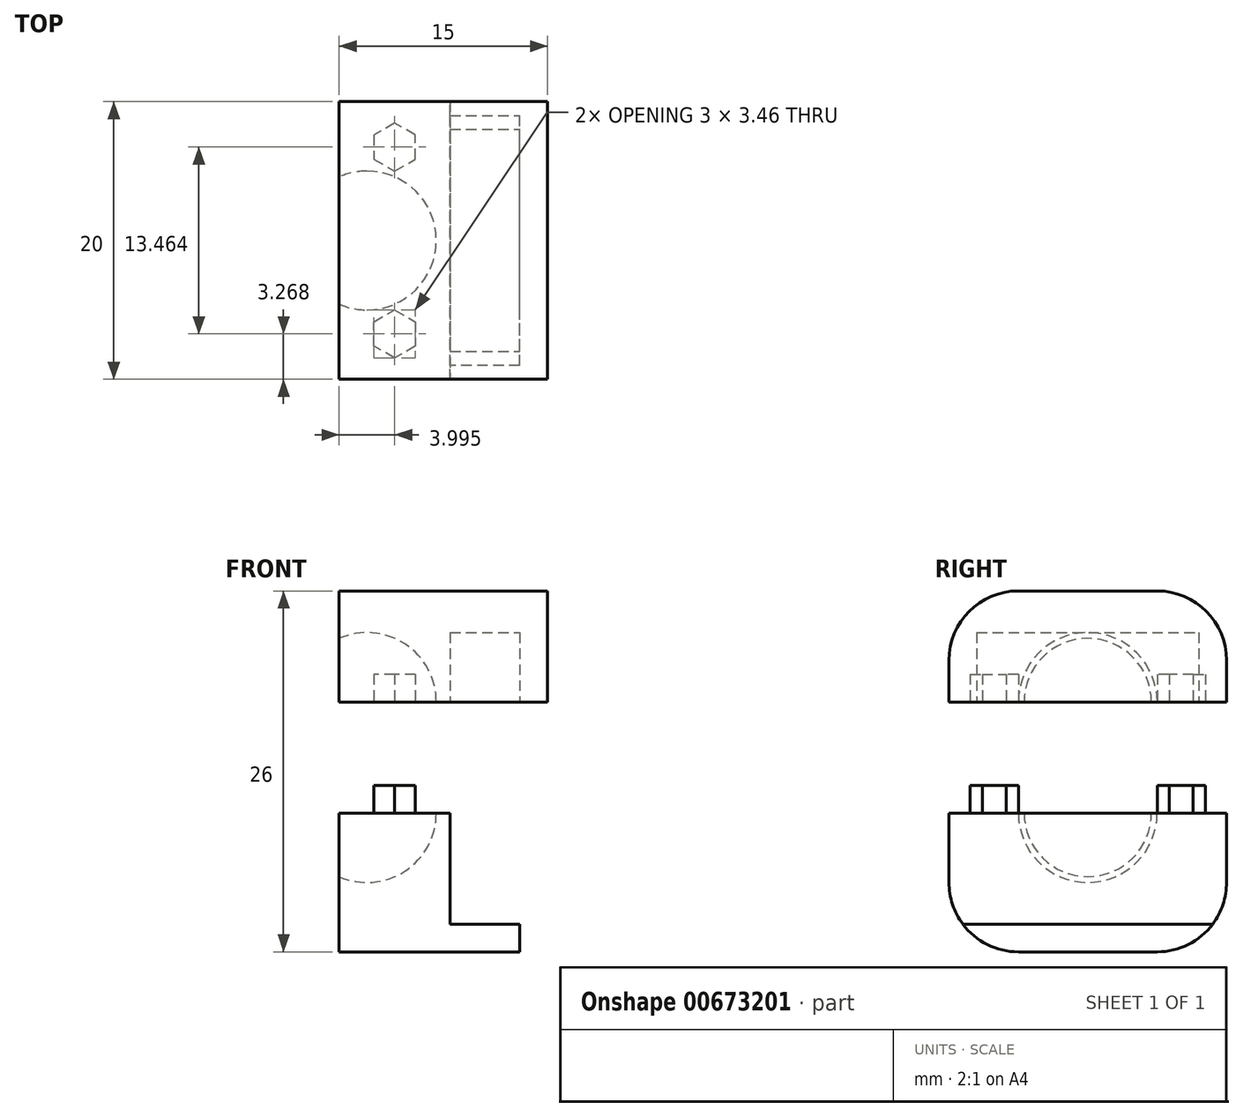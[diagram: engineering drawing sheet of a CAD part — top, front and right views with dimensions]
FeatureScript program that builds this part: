
annotation { "Feature Type Name" : "Feature", "Feature Type Description" : "" }
export const myFeature = defineFeature(function(context is Context, id is Id, definition is map)
    precondition{}
    {
        {
            var Q0;
            Q0=qCreatedBy(makeId("Top.planeOp"),FACE);
            var sketch = newSketch(context, id + "F0", { "sketchPlane" : qUnion([Q0])});
            skLineSegment(sketch, "E0.bottom", {"start": v(-4.65, 0) * mm, "end": v(10.35, 0) * mm});
            skLineSegment(sketch, "E0.top", {"start": v(-4.65, -20) * mm, "end": v(10.35, -20) * mm});
            skLineSegment(sketch, "E0.left", {"start": v(-4.65, 0) * mm, "end": v(-4.65, -20) * mm});
            skLineSegment(sketch, "E0.right", {"start": v(10.35, 0) * mm, "end": v(10.35, -20) * mm});
            skLineSegment(sketch, "E1", {"start": v(10.35, 0) * mm, "end": v(3.35, 0) * mm, "construction": true});
            skLineSegment(sketch, "E2", {"start": v(3.35, 0) * mm, "end": v(3.35, -20) * mm});
            skLineSegment(sketch, "E3", {"start": v(3.35, -20) * mm, "end": v(8.35, -20) * mm, "construction": true});
            skLineSegment(sketch, "E4", {"start": v(8.35, -20) * mm, "end": v(8.35, 0) * mm});
            skLineSegment(sketch, "E5", {"start": v(3.35, 0) * mm, "end": v(3.35, -2) * mm, "construction": true});
            skLineSegment(sketch, "E6", {"start": v(3.35, -2) * mm, "end": v(8.35, -2) * mm});
            skLineSegment(sketch, "E7", {"start": v(10.35, -10) * mm, "end": v(16.36, -10) * mm, "construction": true});
            skLineSegment(sketch, "E8.MirrorCS", {"start": v(3.35, -18) * mm, "end": v(8.35, -18) * mm});
            skLineSegment(sketch, "E9", {"start": v(-4.65, -10) * mm, "end": v(-2.65, -10) * mm, "construction": true});
            skPoint(sketch, "E9.endSnap0", {"position": v(3.35, -10) * mm});
            skArc(sketch, "E10", {"start": v(-4.65, -14.58) * mm, "mid": v(2.35, -10) * mm, "end": v(-4.65, -5.42) * mm});
            skLineSegment(sketch, "E11", {"start": v(-2.65, -15) * mm, "end": v(-2.65, -5) * mm});
            skLineSegment(sketch, "E12", {"start": v(-4.65, -20) * mm, "end": v(-0.65, -20) * mm, "construction": true});
            skLineSegment(sketch, "E13.0", {"start": v(-2.15, -17.6) * mm, "end": v(-2.15, -15.87) * mm});
            skLineSegment(sketch, "E13.1", {"start": v(-2.15, -15.87) * mm, "end": v(-0.65, -15) * mm});
            skLineSegment(sketch, "E13.2", {"start": v(-0.65, -15) * mm, "end": v(0.85, -15.87) * mm});
            skLineSegment(sketch, "E13.3", {"start": v(0.85, -15.87) * mm, "end": v(0.85, -17.6) * mm});
            skLineSegment(sketch, "E13.4", {"start": v(0.85, -17.6) * mm, "end": v(-0.65, -18.46) * mm});
            skLineSegment(sketch, "E13.5", {"start": v(-0.65, -18.46) * mm, "end": v(-2.15, -17.6) * mm});
            skPoint(sketch, "E13.0.midPoint", {"position": v(-2.15, -16.73) * mm});
            skLineSegment(sketch, "E14.MirrorCS", {"start": v(-2.15, -2.4) * mm, "end": v(-2.15, -4.13) * mm});
            skLineSegment(sketch, "E15.MirrorCS", {"start": v(0.85, -2.4) * mm, "end": v(-0.65, -1.54) * mm});
            skLineSegment(sketch, "E16.MirrorCS", {"start": v(-2.15, -4.13) * mm, "end": v(-0.65, -5) * mm});
            skLineSegment(sketch, "E17.MirrorCS", {"start": v(0.85, -4.13) * mm, "end": v(0.85, -2.4) * mm});
            skPoint(sketch, "E18.MirrorP", {"position": v(-2.15, -3.27) * mm});
            skLineSegment(sketch, "E19.MirrorCS", {"start": v(-0.65, -1.54) * mm, "end": v(-2.15, -2.4) * mm});
            skLineSegment(sketch, "E20.MirrorCS", {"start": v(-0.65, -5) * mm, "end": v(0.85, -4.13) * mm});
            skSolve(sketch);
        }
        {
            var Q0;
            Q0=qSketchRegion(id+"F0",true);
            var Q1;
            {var subQ0=sQuery(id+"F0.wireOp",EDGE,"E6");Q1=makeQuery(id+"F0.imprint","IMPRINT",FACE,{"disambiguationData":[TD([[makeQuery(id+"F0.imprint","IMPRINT",EDGE,{"derivedFrom":subQ0}),-1.0]])]});}
            var Q2;
            {var subQ0=sQuery(id+"F0.wireOp",EDGE,"E11");Q2=makeQuery(id+"F0.imprint","IMPRINT",FACE,{"disambiguationData":[TD([[makeQuery(id+"F0.imprint","IMPRINT",EDGE,{"derivedFrom":subQ0}),-1.0]])]});}
            var Q3;
            Q3=makeQuery(id+"F0.imprint","IMPRINT",FACE,{"disambiguationData":[TD([[makeQuery(id+"F0.imprint","IMPRINT",EDGE,{"derivedFrom":sQuery(id+"F0.wireOp",EDGE,"E13.0")}),-1.0]])]});
            var Q4;
            Q4=makeQuery(id+"F0.imprint","IMPRINT",FACE,{"disambiguationData":[TD([[makeQuery(id+"F0.imprint","IMPRINT",EDGE,{"derivedFrom":sQuery(id+"F0.wireOp",EDGE,"E14.MirrorCS")}),1.0]])]});
            extrude(context, id + "F1", {"entities" : qUnion([Q0, Q1, Q2, Q3, Q4]), "depth" : 6 * mm});
        }
        {
            var Q0;
            {var subQ0=sQuery(id+"F0.wireOp",EDGE,"E6");Q0=makeQuery(id+"F0.imprint","IMPRINT",FACE,{"disambiguationData":[TD([[makeQuery(id+"F0.imprint","IMPRINT",EDGE,{"derivedFrom":subQ0}),-1.0]])]});}
            extrude(context, id + "F2", {"entities" : qUnion([Q0]), "operationType" : NewBodyOperationType.REMOVE, "depth" : 5 * mm});
        }
        {
            var Q0;
            {var subQ0=sQuery(id+"F0.wireOp",EDGE,"E11");Q0=makeQuery(id+"F0.imprint","IMPRINT",FACE,{"disambiguationData":[TD([[makeQuery(id+"F0.imprint","IMPRINT",EDGE,{"derivedFrom":subQ0}),-1.0]])]});}
            var Q1;
            Q1=sQuery(id+"F0.wireOp",EDGE,"E11");
            revolve(context, id + "F3", {"operationType" : NewBodyOperationType.REMOVE, "entities" : qUnion([Q0]), "axis" : qUnion([Q1]), "revolveType" : RevolveType.FULL, "oppositeDirection" : true});
        }
        {
            var Q0;
            Q0=makeQuery(id+"F0.imprint","IMPRINT",FACE,{"disambiguationData":[TD([[makeQuery(id+"F0.imprint","IMPRINT",EDGE,{"derivedFrom":sQuery(id+"F0.wireOp",EDGE,"E13.0")}),-1.0]])]});
            var Q1;
            Q1=makeQuery(id+"F0.imprint","IMPRINT",FACE,{"disambiguationData":[TD([[makeQuery(id+"F0.imprint","IMPRINT",EDGE,{"derivedFrom":sQuery(id+"F0.wireOp",EDGE,"E14.MirrorCS")}),1.0]])]});
            extrude(context, id + "F4", {"entities" : qUnion([Q0, Q1]), "operationType" : NewBodyOperationType.REMOVE, "depth" : 2 * mm});
        }
        {
            var Q0;
            Q0=qCreatedBy(makeId("Top.planeOp"),FACE);
            cPlane(context, id + "F5", {"entities" : qUnion([Q0]), "cplaneType" : CPlaneType.OFFSET, "offset" : 4 * mm, "oppositeDirection" : true, "width" : 150 * mm, "height" : 150 * mm});
        }
        {
            var Q0;
            Q0=makeQuery(id+"F1.opExtrude","SWEPT_BODY",BODY,{"disambiguationData":[OSD([sQuery(id+"F0.wireOp",EDGE,"E0.bottom"),sQuery(id+"F0.wireOp",EDGE,"E0.top"),sQuery(id+"F0.wireOp",EDGE,"E0.left"),sQuery(id+"F0.wireOp",EDGE,"E0.right")])]});
            var Q1;
            Q1=qCreatedBy(id+"F5.planeOp",FACE);
            mirror(context, id + "F6", {"entities" : qUnion([Q0]), "mirrorPlane" : qUnion([Q1])});
        }
        {
            var Q0;
            Q0=makeQuery(id+"F6.opPattern","COPY",FACE,{"derivedFrom":makeQuery(id+"F1.opExtrude","CAP_FACE",FACE,{"disambiguationData":[OSD([sQuery(id+"F0.wireOp",EDGE,"E0.bottom"),sQuery(id+"F0.wireOp",EDGE,"E0.top"),sQuery(id+"F0.wireOp",EDGE,"E0.left"),sQuery(id+"F0.wireOp",EDGE,"E0.right")])],"isStart":true}),"instanceName":"1"});
            var sketch = newSketch(context, id + "F7", { "sketchPlane" : qUnion([Q0])});
            skLineSegment(sketch, "E21.bottom", {"start": v(3.35, 0) * mm, "end": v(10.35, 0) * mm});
            skLineSegment(sketch, "E21.top", {"start": v(3.35, -20) * mm, "end": v(10.35, -20) * mm});
            skLineSegment(sketch, "E21.left", {"start": v(3.35, 0) * mm, "end": v(3.35, -20) * mm});
            skLineSegment(sketch, "E21.right", {"start": v(10.35, 0) * mm, "end": v(10.35, -20) * mm});
            skSolve(sketch);
        }
        {
            var Q0;
            Q0=qSketchRegion(id+"F7",true);
            extrude(context, id + "F8", {"entities" : qUnion([Q0]), "operationType" : NewBodyOperationType.REMOVE, "endBound" : BoundingType.THROUGH_ALL, "oppositeDirection" : true, "depth" : 25 * mm});
        }
        {
            var Q0;
            Q0=makeQuery(id+"F6.opPattern","COPY",FACE,{"derivedFrom":makeQuery(id+"F4.boolean.opBoolean","COPY",FACE,{"derivedFrom":makeQuery(id+"F4.opExtrude","CAP_FACE",FACE,{"disambiguationData":[OSD([sQuery(id+"F0.wireOp",EDGE,"E14.MirrorCS"),sQuery(id+"F0.wireOp",EDGE,"E15.MirrorCS"),sQuery(id+"F0.wireOp",EDGE,"E16.MirrorCS"),sQuery(id+"F0.wireOp",EDGE,"E17.MirrorCS"),sQuery(id+"F0.wireOp",EDGE,"E19.MirrorCS"),sQuery(id+"F0.wireOp",EDGE,"E20.MirrorCS")])],"isStart":false})}),"instanceName":"1"});
            var Q1;
            Q1=makeQuery(id+"F6.opPattern","COPY",FACE,{"derivedFrom":makeQuery(id+"F4.boolean.opBoolean","COPY",FACE,{"derivedFrom":makeQuery(id+"F4.opExtrude","CAP_FACE",FACE,{"disambiguationData":[OSD([sQuery(id+"F0.wireOp",EDGE,"E13.0"),sQuery(id+"F0.wireOp",EDGE,"E13.1"),sQuery(id+"F0.wireOp",EDGE,"E13.2"),sQuery(id+"F0.wireOp",EDGE,"E13.3"),sQuery(id+"F0.wireOp",EDGE,"E13.4"),sQuery(id+"F0.wireOp",EDGE,"E13.5")])],"isStart":false})}),"instanceName":"1"});
            extrude(context, id + "F9", {"entities" : qUnion([Q0, Q1]), "operationType" : NewBodyOperationType.ADD, "depth" : 4 * mm});
        }
        {
            var Q0;
            Q0=makeQuery(id+"F6.opPattern","COPY",FACE,{"derivedFrom":makeQuery(id+"F1.opExtrude","CAP_FACE",FACE,{"disambiguationData":[OSD([sQuery(id+"F0.wireOp",EDGE,"E0.bottom"),sQuery(id+"F0.wireOp",EDGE,"E0.top"),sQuery(id+"F0.wireOp",EDGE,"E0.left"),sQuery(id+"F0.wireOp",EDGE,"E0.right")])],"isStart":false}),"instanceName":"1"});
            extrude(context, id + "F10", {"entities" : qUnion([Q0]), "operationType" : NewBodyOperationType.ADD, "depth" : 2 * mm});
        }
        {
            var Q0;
            Q0=makeQuery(id+"F10.opExtrude","CAP_FACE",FACE,{"disambiguationData":[OSD([sQuery(id+"F0.wireOp",EDGE,"E0.bottom"),sQuery(id+"F0.wireOp",EDGE,"E0.top"),sQuery(id+"F0.wireOp",EDGE,"E0.left"),sQuery(id+"F0.wireOp",EDGE,"E0.right")])],"isStart":false});
            extrude(context, id + "F11", {"entities" : qUnion([Q0]), "operationType" : NewBodyOperationType.ADD, "depth" : 2 * mm});
        }
        {
            var Q0;
            {var subQ0=sQuery(id+"F7.wireOp",EDGE,"E21.left");var subQ1=sQuery(id+"F0.wireOp",EDGE,"E0.right");var subQ2=sQuery(id+"F0.wireOp",EDGE,"E0.left");var subQ3=sQuery(id+"F0.wireOp",EDGE,"E0.top");var subQ4=sQuery(id+"F0.wireOp",EDGE,"E0.bottom");Q0=makeQuery(id+"F11.boolean.opBoolean","MERGE",FACE,{"derivedFrom":[makeQuery(id+"F10.boolean.opBoolean","MERGE",FACE,{"derivedFrom":[makeQuery(id+"F8.boolean.opBoolean","MERGE",FACE,{"derivedFrom":[makeQuery(id+"F6.opPattern","COPY",FACE,{"derivedFrom":makeQuery(id+"F2.boolean.opBoolean","COPY",FACE,{"derivedFrom":makeQuery(id+"F2.opExtrude","SWEPT_FACE",FACE,{"disambiguationData":[OSD([sQuery(id+"F0.wireOp",EDGE,"E2")])]})}),"instanceName":"1"}),makeQuery(id+"F8.opExtrude","SWEPT_FACE",FACE,{"disambiguationData":[OSD([subQ0])]})]}),makeQuery(id+"F10.opExtrude","SWEPT_FACE",FACE,{"disambiguationData":[OSD([subQ4,subQ3,subQ2,subQ1,subQ0])]})]}),makeQuery(id+"F11.opExtrude","SWEPT_FACE",FACE,{"disambiguationData":[OSD([subQ4,subQ3,subQ2,subQ1,subQ0])]})]});}
            var sketch = newSketch(context, id + "F12", { "sketchPlane" : qUnion([Q0])});
            skLineSegment(sketch, "E22.bottom", {"start": v(-20, -18) * mm, "end": v(0, -18) * mm});
            skLineSegment(sketch, "E22.top", {"start": v(-20, -16) * mm, "end": v(0, -16) * mm});
            skLineSegment(sketch, "E22.left", {"start": v(-20, -18) * mm, "end": v(-20, -16) * mm});
            skLineSegment(sketch, "E22.right", {"start": v(0, -18) * mm, "end": v(0, -16) * mm});
            skSolve(sketch);
        }
        {
            var Q0;
            Q0=qSketchRegion(id+"F12",true);
            extrude(context, id + "F13", {"entities" : qUnion([Q0]), "operationType" : NewBodyOperationType.ADD, "depth" : 5 * mm});
        }
        {
            var Q0;
            Q0=makeQuery(id+"F1.opExtrude","CAP_FACE",FACE,{"disambiguationData":[OSD([sQuery(id+"F0.wireOp",EDGE,"E0.bottom"),sQuery(id+"F0.wireOp",EDGE,"E0.top"),sQuery(id+"F0.wireOp",EDGE,"E0.left"),sQuery(id+"F0.wireOp",EDGE,"E0.right")])],"isStart":false});
            extrude(context, id + "F14", {"entities" : qUnion([Q0]), "operationType" : NewBodyOperationType.ADD, "depth" : 2 * mm});
        }
        {
            var Q0;
            Q0=makeQuery(id+"F14.opExtrude","CAP_EDGE",EDGE,{"disambiguationData":[OSD([sQuery(id+"F0.wireOp",EDGE,"E0.top")])],"isStart":false});
            var Q1;
            Q1=makeQuery(id+"F14.opExtrude","CAP_EDGE",EDGE,{"disambiguationData":[OSD([sQuery(id+"F0.wireOp",EDGE,"E0.bottom")])],"isStart":false});
            var Q2;
            Q2=makeQuery(id+"F13.boolean.opBoolean","MERGE",EDGE,{"derivedFrom":[makeQuery(id+"F11.opExtrude","CAP_EDGE",EDGE,{"disambiguationData":[OSD([sQuery(id+"F0.wireOp",EDGE,"E0.bottom")])],"isStart":false}),makeQuery(id+"F13.opExtrude","SWEPT_EDGE",EDGE,{"disambiguationData":[OSD([sQuery(id+"F12.wireOp",EDGE,"E22.bottom"),sQuery(id+"F12.wireOp",EDGE,"E22.right")])]})]});
            var Q3;
            Q3=makeQuery(id+"F13.boolean.opBoolean","MERGE",EDGE,{"derivedFrom":[makeQuery(id+"F11.opExtrude","CAP_EDGE",EDGE,{"disambiguationData":[OSD([sQuery(id+"F0.wireOp",EDGE,"E0.top")])],"isStart":false}),makeQuery(id+"F13.opExtrude","SWEPT_EDGE",EDGE,{"disambiguationData":[OSD([sQuery(id+"F12.wireOp",EDGE,"E22.bottom"),sQuery(id+"F12.wireOp",EDGE,"E22.left")])]})]});
            fillet(context, id + "F15", {"entities" : qUnion([Q0, Q1, Q2, Q3]), "radius" : 5 * mm, "tangentPropagation" : true, "allowEdgeOverflow" : false});
        }
    });
